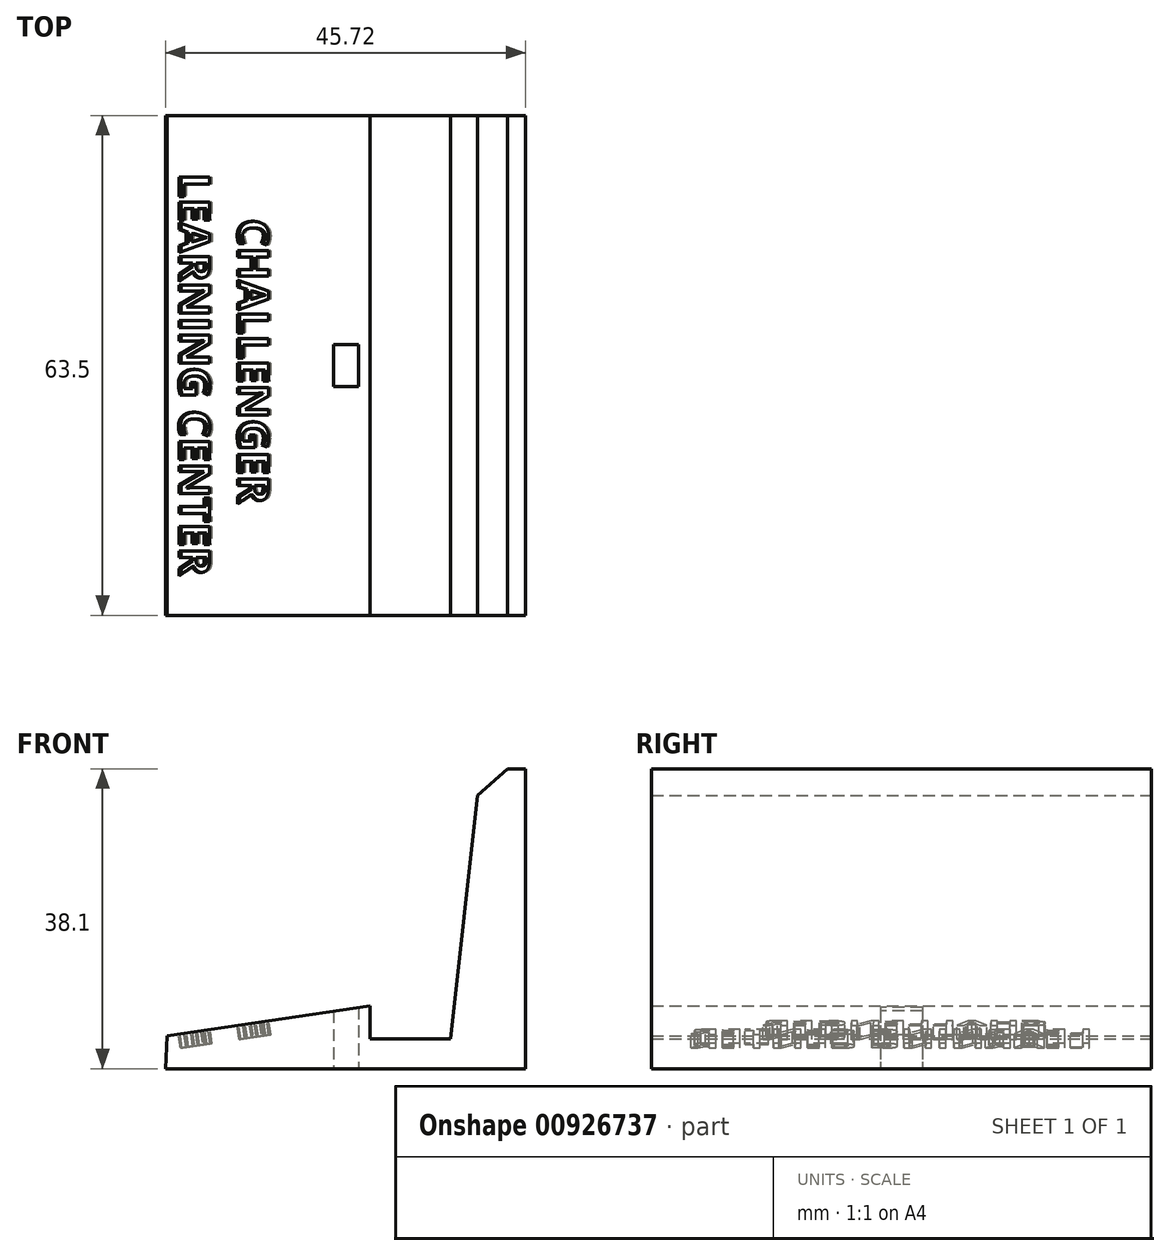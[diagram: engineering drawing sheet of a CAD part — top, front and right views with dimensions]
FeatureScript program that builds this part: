
annotation { "Feature Type Name" : "Feature", "Feature Type Description" : "" }
export const myFeature = defineFeature(function(context is Context, id is Id, definition is map)
    precondition{}
    {
        {
            var Q0;
            Q0=qCreatedBy(makeId("Front.planeOp"),FACE);
            var sketch = newSketch(context, id + "F0", { "sketchPlane" : qUnion([Q0])});
            skLineSegment(sketch, "E0", {"start": v(-18.89, -17.21) * mm, "end": v(6.88, -13.38) * mm});
            skLineSegment(sketch, "E1", {"start": v(17.1, -17.61) * mm, "end": v(20.91, 16.72) * mm});
            skLineSegment(sketch, "E2", {"start": v(20.91, 16.72) * mm, "end": v(26.63, 16.72) * mm});
            skLineSegment(sketch, "E3", {"start": v(26.63, 16.72) * mm, "end": v(26.63, -21.38) * mm});
            skLineSegment(sketch, "E4", {"start": v(26.63, -21.38) * mm, "end": v(-19.09, -21.38) * mm});
            skLineSegment(sketch, "E5", {"start": v(-19.09, -21.38) * mm, "end": v(-18.89, -17.21) * mm});
            skLineSegment(sketch, "E6", {"start": v(6.88, -13.38) * mm, "end": v(6.88, -17.61) * mm});
            skLineSegment(sketch, "E7", {"start": v(6.88, -17.61) * mm, "end": v(17.1, -17.61) * mm});
            skSolve(sketch);
        }
        {
            var Q0;
            Q0 = qSketchRegion(id + "F0", true);
            extrude(context, id + "F1", {"entities" : qUnion([Q0]), "depth" : 63.5 * mm, "offsetDistance" : 25.4 * mm});
        }
        {
            var Q0;
            Q0=makeQuery(id+"F1.opExtrude","SWEPT_FACE",FACE,{"disambiguationData":[OSD([sQuery(id+"F0.wireOp",EDGE,"E0")])]});
            var sketch = newSketch(context, id + "F2", { "sketchPlane" : qUnion([Q0])});
            skText(sketch, "E8", { "text": "    CHALLENGER\nLEARNING CENTER", "fontName": "OpenSans-Bold.ttf"});
            skPoint(sketch, "E9", {"position": v(-8.2, -63.5) * mm});
            const initialGuessF2  = {"E8": [-0.01218, -0.00737, 0, -1, 0.00399]};
            skSetInitialGuess(sketch, initialGuessF2);
            skSolve(sketch);
        }
        {
            var Q0;
            Q0 = qSketchRegion(id + "F2", true);
            extrude(context, id + "F3", {"entities" : qUnion([Q0]), "operationType" : NewBodyOperationType.REMOVE, "oppositeDirection" : true, "depth" : 1.78 * mm, "offsetDistance" : 25.4 * mm});
        }
        {
            var Q0;
            Q0=makeQuery(id+"F1.opExtrude","SWEPT_FACE",FACE,{"disambiguationData":[OSD([sQuery(id+"F0.wireOp",EDGE,"E4")])]});
            var sketch = newSketch(context, id + "F4", { "sketchPlane" : qUnion([Q0])});
            skLineSegment(sketch, "E10.bottom", {"start": v(2.25, 34.42) * mm, "end": v(5.42, 34.42) * mm});
            skLineSegment(sketch, "E10.top", {"start": v(2.25, 29.08) * mm, "end": v(5.42, 29.08) * mm});
            skLineSegment(sketch, "E10.left", {"start": v(2.25, 34.42) * mm, "end": v(2.25, 29.08) * mm});
            skLineSegment(sketch, "E10.right", {"start": v(5.42, 34.42) * mm, "end": v(5.42, 29.08) * mm});
            skPoint(sketch, "E10.middle", {"position": v(3.83, 31.75) * mm});
            skSolve(sketch);
        }
        {
            var Q0;
            Q0 = qSketchRegion(id + "F4", true);
            extrude(context, id + "F5", {"entities" : qUnion([Q0]), "operationType" : NewBodyOperationType.REMOVE, "endBound" : BoundingType.THROUGH_ALL, "oppositeDirection" : true, "depth" : 25.4 * mm, "offsetDistance" : 25.4 * mm});
        }
        {
            var Q0;
            Q0=makeQuery(id+"F1.opExtrude","SWEPT_EDGE",EDGE,{"disambiguationData":[OSD([sQuery(id+"F0.wireOp",EDGE,"E1"),sQuery(id+"F0.wireOp",EDGE,"E2")])]});
            chamfer(context, id + "F6", {"entities" : qUnion([Q0]), "width" : 3.8 * mm, "tangentPropagation" : true});
        }
    });
